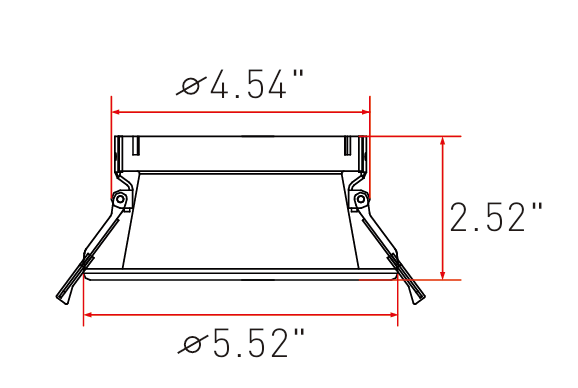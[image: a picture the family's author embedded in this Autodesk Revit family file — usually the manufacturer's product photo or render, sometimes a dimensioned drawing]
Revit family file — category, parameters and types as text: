
# Revit family: Alcon-14123-4R-Revit-Family
name_source: partatom
category: Lighting Fixtures
units: mm (PartAtom-declared; Revit-internal decimal feet)

## family parameters
Always vertical = Yes
Cut with Voids When Loaded = No
Host = Ceiling
Light Source = Yes
OmniClass Number = 23.80.70.11
OmniClass Title = Luminaries for Internal Lighting
Part Type = Normal
Room Calculation Point = No
Round Connector Dimension = Use Diameter
Shared = No

## types (1)
- Type 1
    Color Filter = 16777215
    Default Elevation = 0' - 0"
    Dimming Lamp Color Temperature Shift = <None>
    Housing = <By Category>
    Light Source Symbol Length = 10' - 0"
    LightSource = <By Category>
    Link To Product Page = https://www.alconlighting.com
    Manufacturer = Alcon Light
    Product Identity = Alcon Lighting 14123-4R
    Spot Beam Angle = 30.00°
    Spot Field Angle = 90.00°
    Tilt Angle = 60.00°

## geometry (parser evidence)
native form markers: Sweep x2
no freeform markers — native parametric forms only
